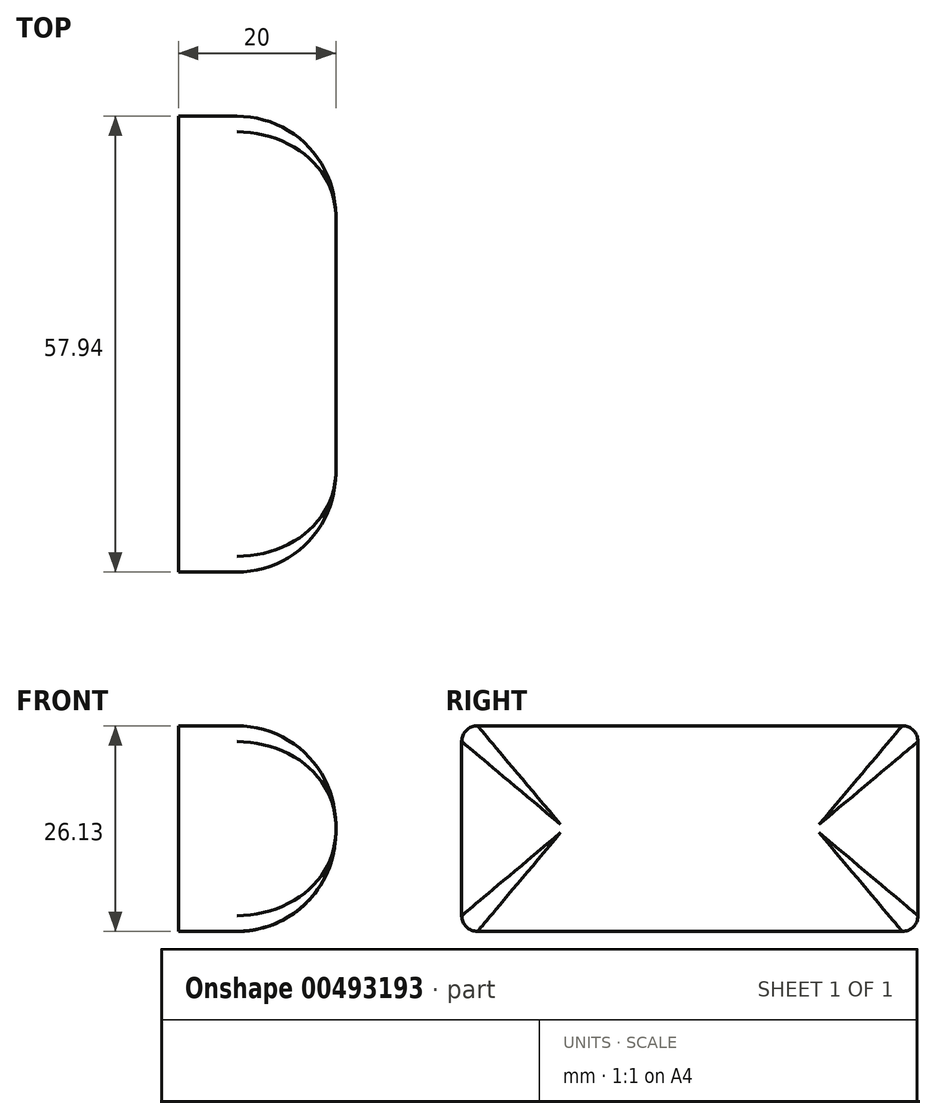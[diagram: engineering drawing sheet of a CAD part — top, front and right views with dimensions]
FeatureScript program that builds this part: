
annotation { "Feature Type Name" : "Feature", "Feature Type Description" : "" }
export const myFeature = defineFeature(function(context is Context, id is Id, definition is map)
    precondition{}
    {
        {
            var Q0;
            Q0=qCreatedBy(makeId("Right.planeOp"),FACE);
            var sketch = newSketch(context, id + "F0", { "sketchPlane" : qUnion([Q0])});
            skLineSegment(sketch, "E0.bottom", {"start": v(-52.5, 44.74) * mm, "end": v(5.44, 44.74) * mm});
            skLineSegment(sketch, "E0.top", {"start": v(-52.5, 18.6) * mm, "end": v(5.44, 18.6) * mm});
            skLineSegment(sketch, "E0.left", {"start": v(-52.5, 44.74) * mm, "end": v(-52.5, 18.6) * mm});
            skLineSegment(sketch, "E0.right", {"start": v(5.44, 44.74) * mm, "end": v(5.44, 18.6) * mm});
            skSolve(sketch);
        }
        {
            var Q0;
            Q0 = qSketchRegion(id + "F0", true);
            extrude(context, id + "F1", {"entities" : qUnion([Q0]), "depth" : 20 * mm});
        }
        {
            var Q0;
            Q0=makeQuery(id+"F1.opExtrude","CAP_EDGE",EDGE,{"disambiguationData":[OSD([sQuery(id+"F0.wireOp",EDGE,"E0.top")])],"isStart":false});
            var Q1;
            Q1=makeQuery(id+"F1.opExtrude","CAP_EDGE",EDGE,{"disambiguationData":[OSD([sQuery(id+"F0.wireOp",EDGE,"E0.right")])],"isStart":false});
            var Q2;
            Q2=makeQuery(id+"F1.opExtrude","CAP_EDGE",EDGE,{"disambiguationData":[OSD([sQuery(id+"F0.wireOp",EDGE,"E0.bottom")])],"isStart":false});
            var Q3;
            Q3=makeQuery(id+"F1.opExtrude","CAP_EDGE",EDGE,{"disambiguationData":[OSD([sQuery(id+"F0.wireOp",EDGE,"E0.left")])],"isStart":false});
            fillet(context, id + "F2", {"entities" : qUnion([Q0, Q1, Q2, Q3]), "radius" : 12.55 * mm, "tangentPropagation" : true, "allowEdgeOverflow" : false});
        }
        {
            var Q0;
            {var subQ0=sQuery(id+"F0.wireOp",EDGE,"E0.top");Q0=makeQuery(id+"F2.opFillet","BLEND_EDGE",EDGE,{"blendedFrom":[makeQuery(id+"F1.opExtrude","CAP_EDGE",EDGE,{"disambiguationData":[OSD([subQ0])],"isStart":false}),makeQuery(id+"F1.opExtrude","CAP_FACE",FACE,{"disambiguationData":[OSD([sQuery(id+"F0.wireOp",EDGE,"E0.bottom"),subQ0,sQuery(id+"F0.wireOp",EDGE,"E0.left"),sQuery(id+"F0.wireOp",EDGE,"E0.right")])],"isStart":false})],"blendedInto":[makeQuery(id+"F1.opExtrude","CAP_FACE",FACE,{"disambiguationData":[OSD([sQuery(id+"F0.wireOp",EDGE,"E0.bottom"),subQ0,sQuery(id+"F0.wireOp",EDGE,"E0.left"),sQuery(id+"F0.wireOp",EDGE,"E0.right")])],"isStart":false})]});}
            var Q1;
            Q1=makeQuery(id+"F2.opFillet","BLEND_EDGE",EDGE,{"blendedFrom":[makeQuery(id+"F1.opExtrude","CAP_EDGE",EDGE,{"disambiguationData":[OSD([sQuery(id+"F0.wireOp",EDGE,"E0.top")])],"isStart":false}),makeQuery(id+"F1.opExtrude","CAP_EDGE",EDGE,{"disambiguationData":[OSD([sQuery(id+"F0.wireOp",EDGE,"E0.left")])],"isStart":false})],"blendedInto":[]});
            var Q2;
            Q2=makeQuery(id+"F2.opFillet","BLEND_EDGE",EDGE,{"blendedFrom":[makeQuery(id+"F1.opExtrude","CAP_EDGE",EDGE,{"disambiguationData":[OSD([sQuery(id+"F0.wireOp",EDGE,"E0.bottom")])],"isStart":false}),makeQuery(id+"F1.opExtrude","CAP_EDGE",EDGE,{"disambiguationData":[OSD([sQuery(id+"F0.wireOp",EDGE,"E0.left")])],"isStart":false})],"blendedInto":[]});
            var Q3;
            Q3=makeQuery(id+"F2.opFillet","BLEND_EDGE",EDGE,{"blendedFrom":[makeQuery(id+"F1.opExtrude","CAP_EDGE",EDGE,{"disambiguationData":[OSD([sQuery(id+"F0.wireOp",EDGE,"E0.top")])],"isStart":false}),makeQuery(id+"F1.opExtrude","CAP_EDGE",EDGE,{"disambiguationData":[OSD([sQuery(id+"F0.wireOp",EDGE,"E0.right")])],"isStart":false})],"blendedInto":[]});
            var Q4;
            Q4=makeQuery(id+"F2.opFillet","BLEND_EDGE",EDGE,{"blendedFrom":[makeQuery(id+"F1.opExtrude","CAP_EDGE",EDGE,{"disambiguationData":[OSD([sQuery(id+"F0.wireOp",EDGE,"E0.bottom")])],"isStart":false}),makeQuery(id+"F1.opExtrude","CAP_EDGE",EDGE,{"disambiguationData":[OSD([sQuery(id+"F0.wireOp",EDGE,"E0.right")])],"isStart":false})],"blendedInto":[]});
            fillet(context, id + "F3", {"entities" : qUnion([Q0, Q1, Q2, Q3, Q4]), "radius" : 2 * mm, "tangentPropagation" : true, "allowEdgeOverflow" : false});
        }
    });
